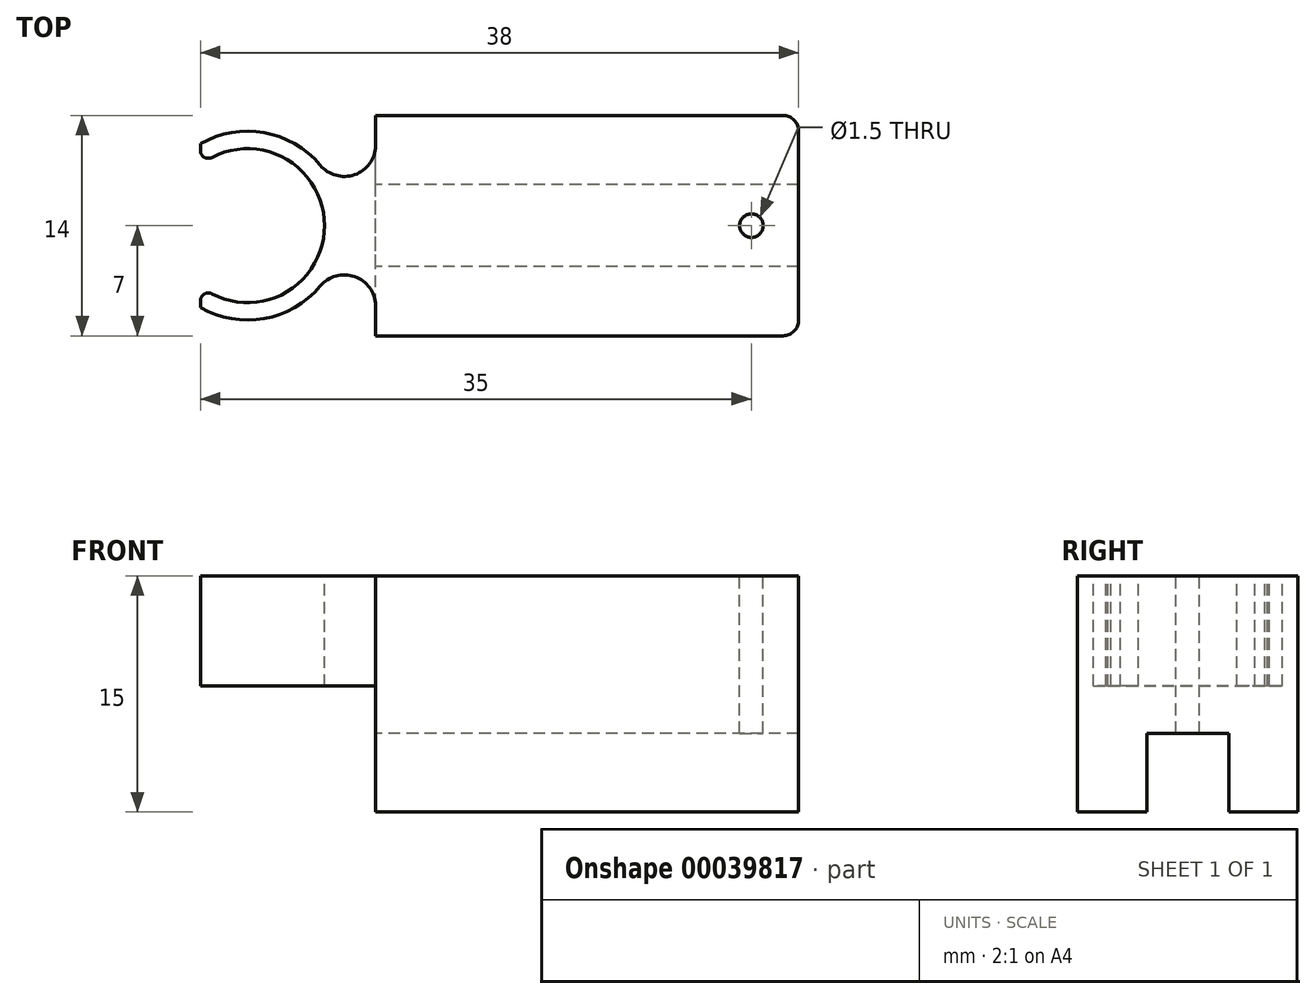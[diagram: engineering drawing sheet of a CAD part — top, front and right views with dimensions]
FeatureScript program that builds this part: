
annotation { "Feature Type Name" : "Feature", "Feature Type Description" : "" }
export const myFeature = defineFeature(function(context is Context, id is Id, definition is map)
    precondition{}
    {
        {
            var Q0;
            Q0=qCreatedBy(makeId("Top.planeOp"),FACE);
            var sketch = newSketch(context, id + "F0", { "sketchPlane" : qUnion([Q0])});
            skLineSegment(sketch, "E0.bottom", {"start": v(0, 0) * mm, "end": v(38, 0) * mm});
            skLineSegment(sketch, "E0.top", {"start": v(0, 14) * mm, "end": v(38, 14) * mm});
            skLineSegment(sketch, "E0.left", {"start": v(0, 0) * mm, "end": v(0, 14) * mm});
            skLineSegment(sketch, "E0.right", {"start": v(38, 0) * mm, "end": v(38, 14) * mm});
            skSolve(sketch);
        }
        {
            var Q0;
            Q0 = qSketchRegion(id + "F0", true);
            extrude(context, id + "F1", {"entities" : qUnion([Q0]), "depth" : 15 * mm});
        }
        {
            var Q0;
            Q0=makeQuery(id+"F1.opExtrude","CAP_FACE",FACE,{"disambiguationData":[OSD([sQuery(id+"F0.wireOp",EDGE,"E0.bottom"),sQuery(id+"F0.wireOp",EDGE,"E0.top"),sQuery(id+"F0.wireOp",EDGE,"E0.left"),sQuery(id+"F0.wireOp",EDGE,"E0.right")])],"isStart":false});
            var sketch = newSketch(context, id + "F2", { "sketchPlane" : qUnion([Q0])});
            skCircle(sketch, "E1", {"center": v(3, 7) * mm, "radius": 4.89 * mm});
            skLineSegment(sketch, "E2", {"start": v(38, 7) * mm, "end": v(-14.05, 7) * mm, "construction": true});
            skSolve(sketch);
        }
        {
            var Q0;
            Q0 = qSketchRegion(id + "F2", true);
            extrude(context, id + "F3", {"entities" : qUnion([Q0]), "operationType" : NewBodyOperationType.REMOVE, "endBound" : BoundingType.THROUGH_ALL, "oppositeDirection" : true, "depth" : 25 * mm});
        }
        {
            var Q0;
            Q0=makeQuery(id+"F1.opExtrude","CAP_FACE",FACE,{"disambiguationData":[OSD([sQuery(id+"F0.wireOp",EDGE,"E0.bottom"),sQuery(id+"F0.wireOp",EDGE,"E0.top"),sQuery(id+"F0.wireOp",EDGE,"E0.left"),sQuery(id+"F0.wireOp",EDGE,"E0.right")])],"isStart":true});
            var sketch = newSketch(context, id + "F4", { "sketchPlane" : qUnion([Q0])});
            skLineSegment(sketch, "E3.bottom", {"start": v(38, -4.4) * mm, "end": v(7.14, -4.4) * mm});
            skLineSegment(sketch, "E3.top", {"start": v(38, -9.6) * mm, "end": v(7.14, -9.6) * mm});
            skLineSegment(sketch, "E3.left", {"start": v(38, -4.4) * mm, "end": v(38, -9.6) * mm});
            skLineSegment(sketch, "E3.right", {"start": v(7.14, -4.4) * mm, "end": v(7.14, -9.6) * mm});
            skLineSegment(sketch, "E4", {"start": v(38, -7) * mm, "end": v(-3.95, -7) * mm, "construction": true});
            skSolve(sketch);
        }
        {
            var Q0;
            Q0 = qSketchRegion(id + "F4", true);
            extrude(context, id + "F5", {"entities" : qUnion([Q0]), "operationType" : NewBodyOperationType.REMOVE, "oppositeDirection" : true, "depth" : 5 * mm});
        }
        {
            var Q0;
            Q0=makeQuery(id+"F1.opExtrude","CAP_FACE",FACE,{"disambiguationData":[OSD([sQuery(id+"F0.wireOp",EDGE,"E0.bottom"),sQuery(id+"F0.wireOp",EDGE,"E0.top"),sQuery(id+"F0.wireOp",EDGE,"E0.left"),sQuery(id+"F0.wireOp",EDGE,"E0.right")])],"isStart":false});
            var sketch = newSketch(context, id + "F6", { "sketchPlane" : qUnion([Q0])});
            skArc(sketch, "E5", {"start": v(0, 1.8) * mm, "mid": v(4.05, 1.1) * mm, "end": v(7.6, 3.16) * mm});
            skLineSegment(sketch, "E6", {"start": v(11.14, 14.9) * mm, "end": v(11.14, 0.23) * mm, "construction": true});
            skArc(sketch, "E7", {"start": v(7.6, 10.84) * mm, "mid": v(9.8, 10.23) * mm, "end": v(11.14, 12.06) * mm});
            skArc(sketch, "E8", {"start": v(11.14, 1.94) * mm, "mid": v(9.8, 3.77) * mm, "end": v(7.6, 3.16) * mm});
            skArc(sketch, "E9", {"start": v(11.14, 12.09) * mm, "mid": v(11.14, 12.08) * mm, "end": v(11.14, 12.06) * mm});
            skArc(sketch, "E10", {"start": v(11.14, 1.94) * mm, "mid": v(11.14, 1.92) * mm, "end": v(11.14, 1.91) * mm});
            skLineSegment(sketch, "E11", {"start": v(0, 12.2) * mm, "end": v(0, 14) * mm});
            skLineSegment(sketch, "E12", {"start": v(0, 14) * mm, "end": v(11.14, 14) * mm});
            skLineSegment(sketch, "E13", {"start": v(0, 0) * mm, "end": v(11.14, 0) * mm});
            skLineSegment(sketch, "E14", {"start": v(0, 0) * mm, "end": v(0, 1.8) * mm});
            skArc(sketch, "E15.trimOffspring", {"start": v(7.6, 10.84) * mm, "mid": v(4.05, 12.9) * mm, "end": v(0, 12.2) * mm});
            skLineSegment(sketch, "E16", {"start": v(11.14, 12.06) * mm, "end": v(11.14, 14) * mm});
            skLineSegment(sketch, "E17", {"start": v(11.14, 1.94) * mm, "end": v(11.14, 0) * mm});
            skSolve(sketch);
        }
        {
            var Q0;
            Q0 = qSketchRegion(id + "F6", true);
            extrude(context, id + "F7", {"entities" : qUnion([Q0]), "operationType" : NewBodyOperationType.REMOVE, "endBound" : BoundingType.THROUGH_ALL, "oppositeDirection" : true, "depth" : 25 * mm});
        }
        {
            var Q0;
            {var subQ1=sQuery(id+"F0.wireOp",EDGE,"E0.right");var subQ3=sQuery(id+"F0.wireOp",EDGE,"E0.bottom");var subQ4=makeQuery(id+"F1.opExtrude","SWEPT_FACE",FACE,{"disambiguationData":[OSD([subQ3])]});var subQ5=sQuery(id+"F0.wireOp",EDGE,"E0.left");Q0=makeQuery(id+"F7.boolean.opBoolean","SPLIT",FACE,{"disambiguationData":[TD([subQ4])],"derivedFrom":makeQuery(id+"F5.boolean.opBoolean","SPLIT",FACE,{"disambiguationData":[TD([subQ4])],"derivedFrom":makeQuery(id+"F1.opExtrude","CAP_FACE",FACE,{"disambiguationData":[OSD([subQ3,sQuery(id+"F0.wireOp",EDGE,"E0.top"),subQ5,subQ1])],"isStart":true})})});}
            var sketch = newSketch(context, id + "F8", { "sketchPlane" : qUnion([Q0])});
            skLineSegment(sketch, "E18", {"start": v(11.14, 0) * mm, "end": v(11.14, -14) * mm});
            skLineSegment(sketch, "E19", {"start": v(11.14, -14) * mm, "end": v(-1.94, -14) * mm});
            skLineSegment(sketch, "E20", {"start": v(-1.94, -14) * mm, "end": v(-1.94, 0) * mm});
            skLineSegment(sketch, "E21", {"start": v(-1.94, 0) * mm, "end": v(11.14, 0) * mm});
            skSolve(sketch);
        }
        {
            var Q0;
            Q0 = qSketchRegion(id + "F8", true);
            extrude(context, id + "F9", {"entities" : qUnion([Q0]), "operationType" : NewBodyOperationType.REMOVE, "oppositeDirection" : true, "depth" : 8 * mm});
        }
        {
            var Q0;
            Q0=makeQuery(id+"F1.opExtrude","CAP_FACE",FACE,{"disambiguationData":[OSD([sQuery(id+"F0.wireOp",EDGE,"E0.bottom"),sQuery(id+"F0.wireOp",EDGE,"E0.top"),sQuery(id+"F0.wireOp",EDGE,"E0.left"),sQuery(id+"F0.wireOp",EDGE,"E0.right")])],"isStart":false});
            var sketch = newSketch(context, id + "F10", { "sketchPlane" : qUnion([Q0])});
            skCircle(sketch, "E22", {"center": v(3, 7) * mm, "radius": 2.54 * mm, "construction": true});
            skLineSegment(sketch, "E23", {"start": v(3, 7) * mm, "end": v(35, 7) * mm, "construction": true});
            skLineSegment(sketch, "E24", {"start": v(35, 0) * mm, "end": v(35, 7) * mm, "construction": true});
            skLineSegment(sketch, "E25", {"start": v(35, 1.03) * mm, "end": v(33.97, 0) * mm});
            skLineSegment(sketch, "E26", {"start": v(35, 1.03) * mm, "end": v(36.03, 0) * mm});
            skLineSegment(sketch, "E27", {"start": v(33.97, 0) * mm, "end": v(36.03, 0) * mm});
            skLineSegment(sketch, "E28.MirrorCS", {"start": v(35, 12.97) * mm, "end": v(33.97, 14) * mm});
            skLineSegment(sketch, "E29.MirrorCS", {"start": v(35, 12.97) * mm, "end": v(36.03, 14) * mm});
            skLineSegment(sketch, "E30.MirrorCS", {"start": v(33.97, 14) * mm, "end": v(36.03, 14) * mm});
            skSolve(sketch);
        }
        {
            var Q0;
            {var subQ12=sQuery(id+"F10.wireOp",EDGE,"E25");Q0=makeQuery(id+"F10.imprint","IMPRINT",FACE,{"disambiguationData":[TD([[makeQuery(id+"F10.imprint","IMPRINT",EDGE,{"derivedFrom":subQ12}),-1.0]])]});}
            var sketch = newSketch(context, id + "F11", { "sketchPlane" : qUnion([Q0])});
            skCircle(sketch, "E31", {"center": v(35, 7) * mm, "radius": 0.75 * mm});
            skSolve(sketch);
        }
        {
            var Q0;
            Q0 = qSketchRegion(id + "F11", true);
            extrude(context, id + "F12", {"entities" : qUnion([Q0]), "operationType" : NewBodyOperationType.REMOVE, "endBound" : BoundingType.THROUGH_ALL, "oppositeDirection" : true, "depth" : 2 * mm});
        }
        {
            var Q0;
            Q0=makeQuery(id+"F3.boolean.opBoolean","INTERSECT",EDGE,{"disambiguationData":[OD(1.0)],"derivedFrom":[makeQuery(id+"F1.opExtrude","SWEPT_FACE",FACE,{"disambiguationData":[OSD([sQuery(id+"F0.wireOp",EDGE,"E0.left")])]}),makeQuery(id+"F3.opExtrude","SWEPT_FACE",FACE,{"disambiguationData":[OSD([sQuery(id+"F2.wireOp",EDGE,"E1")])]})]});
            var Q1;
            Q1=makeQuery(id+"F3.boolean.opBoolean","INTERSECT",EDGE,{"disambiguationData":[OD(0.0)],"derivedFrom":[makeQuery(id+"F1.opExtrude","SWEPT_FACE",FACE,{"disambiguationData":[OSD([sQuery(id+"F0.wireOp",EDGE,"E0.left")])]}),makeQuery(id+"F3.opExtrude","SWEPT_FACE",FACE,{"disambiguationData":[OSD([sQuery(id+"F2.wireOp",EDGE,"E1")])]})]});
            fillet(context, id + "F13", {"entities" : qUnion([Q0, Q1]), "radius" : .5 * mm, "tangentPropagation" : true, "allowEdgeOverflow" : false});
        }
        {
            var Q0;
            Q0=makeQuery(id+"F7.boolean.opBoolean","COPY",EDGE,{"derivedFrom":makeQuery(id+"F7.opExtrude","SWEPT_EDGE",EDGE,{"disambiguationData":[OSD([sQuery(id+"F0.wireOp",EDGE,"E0.bottom"),sQuery(id+"F6.wireOp",EDGE,"E13"),sQuery(id+"F6.wireOp",EDGE,"E17")])]})});
            var Q1;
            Q1=makeQuery(id+"F1.opExtrude","SWEPT_EDGE",EDGE,{"disambiguationData":[OSD([sQuery(id+"F0.wireOp",EDGE,"E0.bottom"),sQuery(id+"F0.wireOp",EDGE,"E0.right")])]});
            var Q2;
            {var subQ0=sQuery(id+"F0.wireOp",EDGE,"E0.top");var subQ1=sQuery(id+"F6.wireOp",EDGE,"E16");Q2=makeQuery(id+"F9.boolean.opBoolean","SPLIT",EDGE,{"disambiguationData":[TD([makeQuery(id+"F1.opExtrude","CAP_FACE",FACE,{"disambiguationData":[OSD([sQuery(id+"F0.wireOp",EDGE,"E0.bottom"),subQ0,sQuery(id+"F0.wireOp",EDGE,"E0.left"),sQuery(id+"F0.wireOp",EDGE,"E0.right")])],"isStart":true})])],"derivedFrom":makeQuery(id+"F7.boolean.opBoolean","COPY",EDGE,{"derivedFrom":makeQuery(id+"F7.opExtrude","SWEPT_EDGE",EDGE,{"disambiguationData":[OSD([sQuery(id+"F6.wireOp",EDGE,"E12"),subQ1])]})})});}
            var Q3;
            Q3=makeQuery(id+"F1.opExtrude","SWEPT_EDGE",EDGE,{"disambiguationData":[OSD([sQuery(id+"F0.wireOp",EDGE,"E0.top"),sQuery(id+"F0.wireOp",EDGE,"E0.right")])]});
            fillet(context, id + "F14", {"entities" : qUnion([Q0, Q1, Q2, Q3]), "radius" : 1 * mm, "tangentPropagation" : true, "allowEdgeOverflow" : false});
        }
    });
